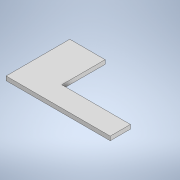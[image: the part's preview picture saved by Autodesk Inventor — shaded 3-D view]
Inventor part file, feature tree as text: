
AUTODESK INVENTOR PART (.ipt)
format: ipt  version: 2020 (Build 240168000, 168)  size: 97,280 bytes
history: native  units: mm
features: other x1, extrude x1, sketch x1
ambient origin geometry x8: Origin, YZ Plane, XZ Plane, XY Plane, X Axis, Y Axis, Z Axis, Center Point
bodies: Body1 (feature_tree)
feature tree (3):
  other  "Bryła1"
  extrude  "Wyciągnięcie proste1"  Depth=35.0mm
  sketch  "Szkic1"
